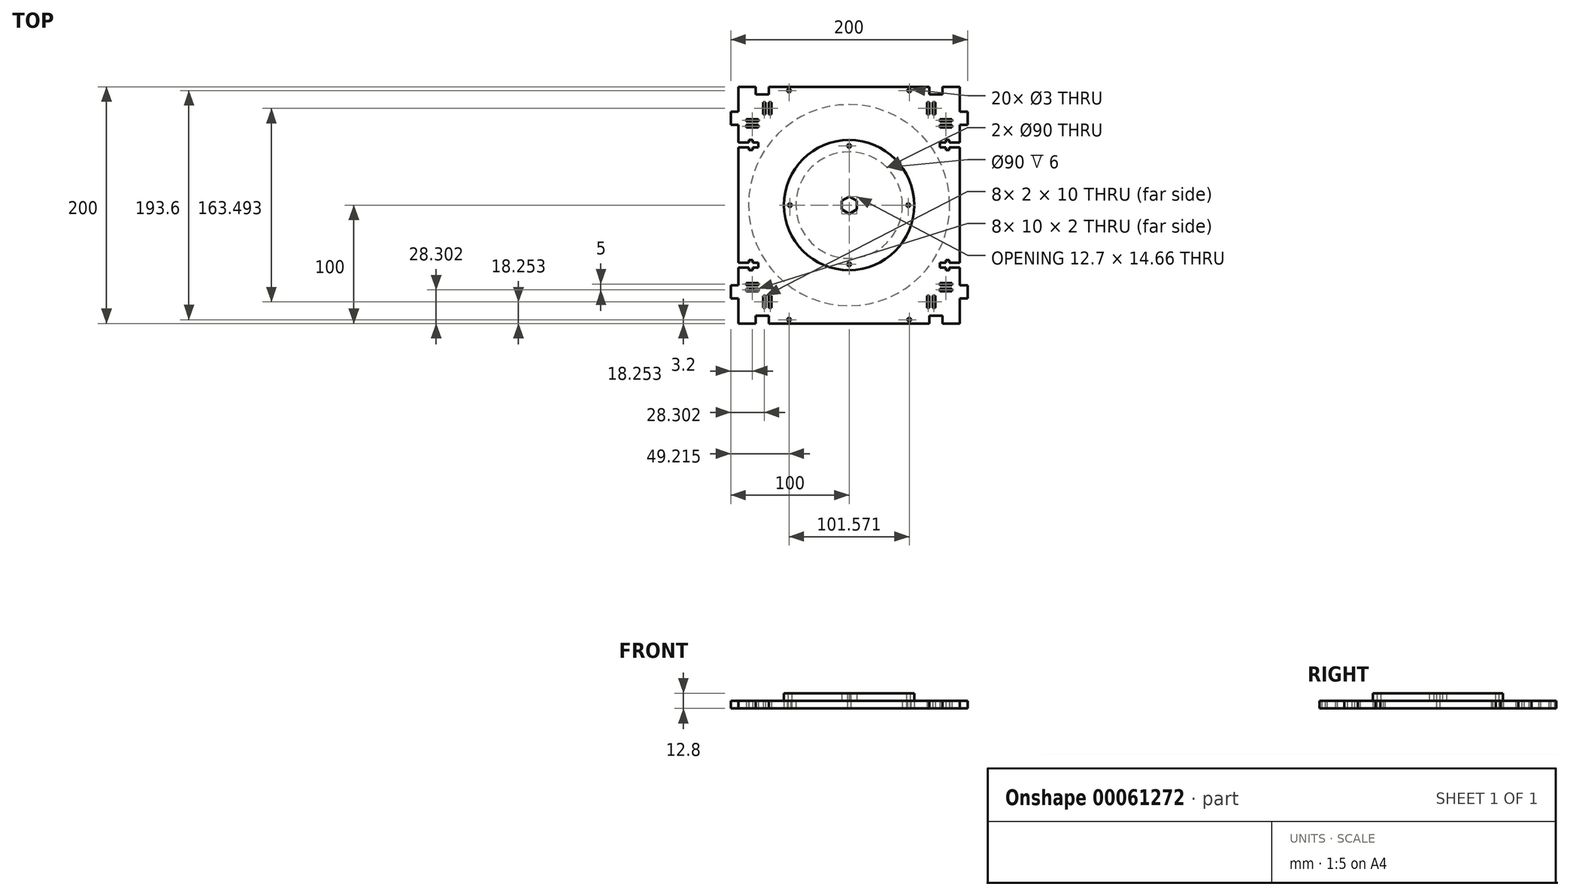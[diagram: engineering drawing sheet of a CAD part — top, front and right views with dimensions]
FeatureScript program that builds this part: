
annotation { "Feature Type Name" : "Feature", "Feature Type Description" : "" }
export const myFeature = defineFeature(function(context is Context, id is Id, definition is map)
    precondition{}
    {
        {
            var Q0;
            Q0=qCreatedBy(makeId("Top.planeOp"),FACE);
            var sketch = newSketch(context, id + "F0", { "sketchPlane" : qUnion([Q0])});
            skLineSegment(sketch, "E0.rect.bottom", {"start": v(100, 100) * mm, "end": v(-100, 100) * mm});
            skLineSegment(sketch, "E0.rect.top", {"start": v(100, -100) * mm, "end": v(-100, -100) * mm});
            skPoint(sketch, "E0.rect.middle", {"position": v(0, 0) * mm});
            skCircle(sketch, "E1", {"center": v(0, 0) * mm, "radius": 55 * mm});
            skCircle(sketch, "E2", {"center": v(0, 0) * mm, "radius": 85 * mm});
            skCircle(sketch, "E3", {"center": v(-50, 0) * mm, "radius": 1.5 * mm});
            skLineSegment(sketch, "E4", {"start": v(-55, 0) * mm, "end": v(-45, 0) * mm, "construction": true});
            skCircle(sketch, "E5.1.0", {"center": v(0, -50) * mm, "radius": 1.5 * mm});
            skCircle(sketch, "E5.2.0", {"center": v(50, 0) * mm, "radius": 1.5 * mm});
            skCircle(sketch, "E6.1.3.0", {"center": v(0, 50) * mm, "radius": 1.5 * mm});
            skLineSegment(sketch, "E7.left", {"start": v(-72.7, -76.75) * mm, "end": v(-72.7, -86.75) * mm});
            skLineSegment(sketch, "E7.right", {"start": v(-65.7, -76.75) * mm, "end": v(-65.7, -86.75) * mm});
            skLineSegment(sketch, "E8", {"start": v(0, 0) * mm, "end": v(-100, -100) * mm, "construction": true});
            skLineSegment(sketch, "E9", {"start": v(-72.7, -76.75) * mm, "end": v(-70.7, -76.75) * mm});
            skLineSegment(sketch, "E10", {"start": v(-70.7, -76.75) * mm, "end": v(-70.7, -86.75) * mm});
            skLineSegment(sketch, "E11", {"start": v(-70.7, -86.75) * mm, "end": v(-72.7, -86.75) * mm});
            skLineSegment(sketch, "E12", {"start": v(-65.7, -76.75) * mm, "end": v(-67.7, -76.75) * mm});
            skLineSegment(sketch, "E13", {"start": v(-67.7, -76.75) * mm, "end": v(-67.7, -86.75) * mm});
            skLineSegment(sketch, "E14", {"start": v(-67.7, -86.75) * mm, "end": v(-65.7, -86.75) * mm});
            skLineSegment(sketch, "E15.MirrorCS", {"start": v(-76.75, -72.7) * mm, "end": v(-76.75, -70.7) * mm});
            skLineSegment(sketch, "E16.MirrorCS", {"start": v(-76.75, -65.7) * mm, "end": v(-76.75, -67.7) * mm});
            skLineSegment(sketch, "E17.MirrorCS", {"start": v(-76.75, -65.7) * mm, "end": v(-86.75, -65.7) * mm});
            skLineSegment(sketch, "E18.MirrorCS", {"start": v(-76.75, -72.7) * mm, "end": v(-86.75, -72.7) * mm});
            skLineSegment(sketch, "E19.MirrorCS", {"start": v(-86.75, -67.7) * mm, "end": v(-86.75, -65.7) * mm});
            skLineSegment(sketch, "E20.MirrorCS", {"start": v(-76.75, -70.7) * mm, "end": v(-86.75, -70.7) * mm});
            skLineSegment(sketch, "E21.MirrorCS", {"start": v(-76.75, -67.7) * mm, "end": v(-86.75, -67.7) * mm});
            skLineSegment(sketch, "E22.MirrorCS", {"start": v(-86.75, -70.7) * mm, "end": v(-86.75, -72.7) * mm});
            skLineSegment(sketch, "E23.1.0", {"start": v(76.75, -65.7) * mm, "end": v(86.75, -65.7) * mm});
            skLineSegment(sketch, "E23.1.1", {"start": v(67.7, -76.75) * mm, "end": v(67.7, -86.75) * mm});
            skLineSegment(sketch, "E23.1.2", {"start": v(72.7, -76.75) * mm, "end": v(72.7, -86.75) * mm});
            skLineSegment(sketch, "E23.1.3", {"start": v(76.75, -72.7) * mm, "end": v(86.75, -72.7) * mm});
            skLineSegment(sketch, "E23.1.4", {"start": v(70.7, -76.75) * mm, "end": v(70.7, -86.75) * mm});
            skLineSegment(sketch, "E23.1.5", {"start": v(76.75, -67.7) * mm, "end": v(86.75, -67.7) * mm});
            skLineSegment(sketch, "E23.1.6", {"start": v(65.7, -76.75) * mm, "end": v(65.7, -86.75) * mm});
            skLineSegment(sketch, "E23.1.7", {"start": v(76.75, -70.7) * mm, "end": v(86.75, -70.7) * mm});
            skLineSegment(sketch, "E23.1.8", {"start": v(67.7, -86.75) * mm, "end": v(65.7, -86.75) * mm});
            skLineSegment(sketch, "E23.1.9", {"start": v(65.7, -76.75) * mm, "end": v(67.7, -76.75) * mm});
            skLineSegment(sketch, "E23.1.10", {"start": v(70.7, -86.75) * mm, "end": v(72.7, -86.75) * mm});
            skLineSegment(sketch, "E23.1.11", {"start": v(76.75, -72.7) * mm, "end": v(76.75, -70.7) * mm});
            skLineSegment(sketch, "E23.1.12", {"start": v(76.75, -65.7) * mm, "end": v(76.75, -67.7) * mm});
            skLineSegment(sketch, "E23.1.13", {"start": v(72.7, -76.75) * mm, "end": v(70.7, -76.75) * mm});
            skLineSegment(sketch, "E23.1.14", {"start": v(86.75, -70.7) * mm, "end": v(86.75, -72.7) * mm});
            skLineSegment(sketch, "E23.1.15", {"start": v(86.75, -67.7) * mm, "end": v(86.75, -65.7) * mm});
            skLineSegment(sketch, "E23.2.0", {"start": v(65.7, 76.75) * mm, "end": v(65.7, 86.75) * mm});
            skLineSegment(sketch, "E23.2.1", {"start": v(76.75, 67.7) * mm, "end": v(86.75, 67.7) * mm});
            skLineSegment(sketch, "E23.2.2", {"start": v(76.75, 72.7) * mm, "end": v(86.75, 72.7) * mm});
            skLineSegment(sketch, "E23.2.3", {"start": v(72.7, 76.75) * mm, "end": v(72.7, 86.75) * mm});
            skLineSegment(sketch, "E23.2.4", {"start": v(76.75, 70.7) * mm, "end": v(86.75, 70.7) * mm});
            skLineSegment(sketch, "E23.2.5", {"start": v(67.7, 76.75) * mm, "end": v(67.7, 86.75) * mm});
            skLineSegment(sketch, "E23.2.6", {"start": v(76.75, 65.7) * mm, "end": v(86.75, 65.7) * mm});
            skLineSegment(sketch, "E23.2.7", {"start": v(70.7, 76.75) * mm, "end": v(70.7, 86.75) * mm});
            skLineSegment(sketch, "E23.2.8", {"start": v(86.75, 67.7) * mm, "end": v(86.75, 65.7) * mm});
            skLineSegment(sketch, "E23.2.9", {"start": v(76.75, 65.7) * mm, "end": v(76.75, 67.7) * mm});
            skLineSegment(sketch, "E23.2.10", {"start": v(86.75, 70.7) * mm, "end": v(86.75, 72.7) * mm});
            skLineSegment(sketch, "E23.2.11", {"start": v(72.7, 76.75) * mm, "end": v(70.7, 76.75) * mm});
            skLineSegment(sketch, "E23.2.12", {"start": v(65.7, 76.75) * mm, "end": v(67.7, 76.75) * mm});
            skLineSegment(sketch, "E23.2.13", {"start": v(76.75, 72.7) * mm, "end": v(76.75, 70.7) * mm});
            skLineSegment(sketch, "E23.2.14", {"start": v(70.7, 86.75) * mm, "end": v(72.7, 86.75) * mm});
            skLineSegment(sketch, "E23.2.15", {"start": v(67.7, 86.75) * mm, "end": v(65.7, 86.75) * mm});
            skLineSegment(sketch, "E23.3.0", {"start": v(-76.75, 65.7) * mm, "end": v(-86.75, 65.7) * mm});
            skLineSegment(sketch, "E23.3.1", {"start": v(-67.7, 76.75) * mm, "end": v(-67.7, 86.75) * mm});
            skLineSegment(sketch, "E23.3.2", {"start": v(-72.7, 76.75) * mm, "end": v(-72.7, 86.75) * mm});
            skLineSegment(sketch, "E23.3.3", {"start": v(-76.75, 72.7) * mm, "end": v(-86.75, 72.7) * mm});
            skLineSegment(sketch, "E23.3.4", {"start": v(-70.7, 76.75) * mm, "end": v(-70.7, 86.75) * mm});
            skLineSegment(sketch, "E23.3.5", {"start": v(-76.75, 67.7) * mm, "end": v(-86.75, 67.7) * mm});
            skLineSegment(sketch, "E23.3.6", {"start": v(-65.7, 76.75) * mm, "end": v(-65.7, 86.75) * mm});
            skLineSegment(sketch, "E23.3.7", {"start": v(-76.75, 70.7) * mm, "end": v(-86.75, 70.7) * mm});
            skLineSegment(sketch, "E23.3.8", {"start": v(-67.7, 86.75) * mm, "end": v(-65.7, 86.75) * mm});
            skLineSegment(sketch, "E23.3.9", {"start": v(-65.7, 76.75) * mm, "end": v(-67.7, 76.75) * mm});
            skLineSegment(sketch, "E23.3.10", {"start": v(-70.7, 86.75) * mm, "end": v(-72.7, 86.75) * mm});
            skLineSegment(sketch, "E23.3.11", {"start": v(-76.75, 72.7) * mm, "end": v(-76.75, 70.7) * mm});
            skLineSegment(sketch, "E23.3.12", {"start": v(-76.75, 65.7) * mm, "end": v(-76.75, 67.7) * mm});
            skLineSegment(sketch, "E23.3.13", {"start": v(-72.7, 76.75) * mm, "end": v(-70.7, 76.75) * mm});
            skLineSegment(sketch, "E23.3.14", {"start": v(-86.75, 70.7) * mm, "end": v(-86.75, 72.7) * mm});
            skLineSegment(sketch, "E23.3.15", {"start": v(-86.75, 67.7) * mm, "end": v(-86.75, 65.7) * mm});
            skCircle(sketch, "E24", {"center": v(0, 0) * mm, "radius": 45 * mm});
            skLineSegment(sketch, "E25", {"start": v(-79, 100) * mm, "end": v(-79, 93.6) * mm});
            skLineSegment(sketch, "E26", {"start": v(-79, 93.6) * mm, "end": v(-67.81, 93.6) * mm});
            skLineSegment(sketch, "E27", {"start": v(-67.81, 93.6) * mm, "end": v(-67.81, 100) * mm});
            skLineSegment(sketch, "E28", {"start": v(0, 0) * mm, "end": v(0, 100) * mm, "construction": true});
            skLineSegment(sketch, "E29.MirrorCS", {"start": v(67.81, 93.6) * mm, "end": v(67.81, 100) * mm});
            skLineSegment(sketch, "E30.MirrorCS", {"start": v(79, 93.6) * mm, "end": v(67.81, 93.6) * mm});
            skLineSegment(sketch, "E31.MirrorCS", {"start": v(79, 100) * mm, "end": v(79, 93.6) * mm});
            skLineSegment(sketch, "E32.1.2", {"start": v(-93.6, 67.81) * mm, "end": v(-100, 67.81) * mm});
            skLineSegment(sketch, "E32.1.3", {"start": v(-100, -79) * mm, "end": v(-93.6, -79) * mm});
            skLineSegment(sketch, "E32.1.4", {"start": v(-100, 79) * mm, "end": v(-93.6, 79) * mm});
            skLineSegment(sketch, "E32.1.5", {"start": v(-93.6, -67.81) * mm, "end": v(-100, -67.81) * mm});
            skLineSegment(sketch, "E32.2.0", {"start": v(-79, -93.6) * mm, "end": v(-67.81, -93.6) * mm});
            skLineSegment(sketch, "E32.2.1", {"start": v(79, -93.6) * mm, "end": v(67.81, -93.6) * mm});
            skLineSegment(sketch, "E32.2.2", {"start": v(-67.81, -93.6) * mm, "end": v(-67.81, -100) * mm});
            skLineSegment(sketch, "E32.2.3", {"start": v(79, -100) * mm, "end": v(79, -93.6) * mm});
            skLineSegment(sketch, "E32.2.4", {"start": v(-79, -100) * mm, "end": v(-79, -93.6) * mm});
            skLineSegment(sketch, "E32.2.5", {"start": v(67.81, -93.6) * mm, "end": v(67.81, -100) * mm});
            skLineSegment(sketch, "E32.3.2", {"start": v(93.6, -67.81) * mm, "end": v(100, -67.81) * mm});
            skLineSegment(sketch, "E32.3.3", {"start": v(100, 79) * mm, "end": v(93.6, 79) * mm});
            skLineSegment(sketch, "E32.3.4", {"start": v(100, -79) * mm, "end": v(93.6, -79) * mm});
            skLineSegment(sketch, "E32.3.5", {"start": v(93.6, 67.81) * mm, "end": v(100, 67.81) * mm});
            skLineSegment(sketch, "E33", {"start": v(-100, 79) * mm, "end": v(-100, 67.81) * mm});
            skLineSegment(sketch, "E34", {"start": v(-100, -67.81) * mm, "end": v(-100, -79) * mm});
            skLineSegment(sketch, "E35", {"start": v(100, -79) * mm, "end": v(100, -67.81) * mm});
            skLineSegment(sketch, "E36", {"start": v(100, 67.81) * mm, "end": v(100, 79) * mm});
            skLineSegment(sketch, "E37", {"start": v(93.6, 67.81) * mm, "end": v(93.6, -67.81) * mm});
            skLineSegment(sketch, "E38", {"start": v(93.6, -79) * mm, "end": v(93.6, -100) * mm});
            skLineSegment(sketch, "E39", {"start": v(93.6, 79) * mm, "end": v(93.6, 100) * mm});
            skLineSegment(sketch, "E40", {"start": v(-93.6, 79) * mm, "end": v(-93.6, 100) * mm});
            skLineSegment(sketch, "E41", {"start": v(-93.6, 67.81) * mm, "end": v(-93.6, -67.81) * mm});
            skLineSegment(sketch, "E42", {"start": v(-93.6, -79) * mm, "end": v(-93.6, -100) * mm});
            skLineSegment(sketch, "E43.MirrorCS", {"start": v(81.6, -48.79) * mm, "end": v(81.6, -46.42) * mm});
            skLineSegment(sketch, "E44.MirrorCS", {"start": v(81.6, -46.42) * mm, "end": v(84.58, -46.42) * mm});
            skLineSegment(sketch, "E45.MirrorCS", {"start": v(76.6, -52.79) * mm, "end": v(76.6, -48.79) * mm});
            skLineSegment(sketch, "E46.MirrorCS", {"start": v(84.58, -55.15) * mm, "end": v(81.6, -55.15) * mm});
            skLineSegment(sketch, "E47.MirrorCS", {"start": v(84.58, -52.79) * mm, "end": v(84.58, -55.15) * mm});
            skLineSegment(sketch, "E48.MirrorCS", {"start": v(84.58, -46.42) * mm, "end": v(84.58, -48.79) * mm});
            skLineSegment(sketch, "E49.MirrorCS", {"start": v(81.6, -55.15) * mm, "end": v(81.6, -52.79) * mm});
            skLineSegment(sketch, "E50.MirrorCS", {"start": v(76.6, -48.79) * mm, "end": v(81.6, -48.79) * mm});
            skLineSegment(sketch, "E51.MirrorCS", {"start": v(84.58, -48.79) * mm, "end": v(93.6, -48.79) * mm});
            skLineSegment(sketch, "E52.MirrorCS", {"start": v(81.6, -52.79) * mm, "end": v(76.6, -52.79) * mm});
            skLineSegment(sketch, "E53.MirrorCS", {"start": v(93.6, -52.79) * mm, "end": v(84.58, -52.79) * mm});
            skLineSegment(sketch, "E54", {"start": v(-93.6, 0) * mm, "end": v(93.6, 0) * mm, "construction": true});
            skLineSegment(sketch, "E55", {"start": v(93.6, -48.79) * mm, "end": v(93.6, -52.79) * mm});
            skLineSegment(sketch, "E56.MirrorCS", {"start": v(93.6, 52.79) * mm, "end": v(84.58, 52.79) * mm});
            skLineSegment(sketch, "E57.MirrorCS", {"start": v(81.6, 55.15) * mm, "end": v(81.6, 52.79) * mm});
            skLineSegment(sketch, "E58.MirrorCS", {"start": v(81.6, 48.79) * mm, "end": v(81.6, 46.42) * mm});
            skLineSegment(sketch, "E59.MirrorCS", {"start": v(76.6, 48.79) * mm, "end": v(81.6, 48.79) * mm});
            skLineSegment(sketch, "E60.MirrorCS", {"start": v(84.58, 48.79) * mm, "end": v(93.6, 48.79) * mm});
            skLineSegment(sketch, "E61.MirrorCS", {"start": v(81.6, 52.79) * mm, "end": v(76.6, 52.79) * mm});
            skLineSegment(sketch, "E62.MirrorCS", {"start": v(84.58, 55.15) * mm, "end": v(81.6, 55.15) * mm});
            skLineSegment(sketch, "E63.MirrorCS", {"start": v(76.6, 52.79) * mm, "end": v(76.6, 48.79) * mm});
            skLineSegment(sketch, "E64.MirrorCS", {"start": v(84.58, 52.79) * mm, "end": v(84.58, 55.15) * mm});
            skLineSegment(sketch, "E65.MirrorCS", {"start": v(93.6, 48.79) * mm, "end": v(93.6, 52.79) * mm});
            skLineSegment(sketch, "E66.MirrorCS", {"start": v(84.58, 46.42) * mm, "end": v(84.58, 48.79) * mm});
            skLineSegment(sketch, "E67.MirrorCS", {"start": v(81.6, 46.42) * mm, "end": v(84.58, 46.42) * mm});
            skPoint(sketch, "E68", {"position": v(93.6, 0) * mm});
            skCircle(sketch, "E69", {"center": v(-50.79, 96.8) * mm, "radius": 1.5 * mm});
            skPoint(sketch, "E70", {"position": v(-67.81, 96.8) * mm});
            skLineSegment(sketch, "E71", {"start": v(-50.79, 96.8) * mm, "end": v(-67.81, 96.8) * mm, "construction": true});
            skLineSegment(sketch, "E72.MirrorCS", {"start": v(-84.58, 48.79) * mm, "end": v(-93.6, 48.79) * mm});
            skLineSegment(sketch, "E73.MirrorCS", {"start": v(-81.6, 46.42) * mm, "end": v(-84.58, 46.42) * mm});
            skLineSegment(sketch, "E74.MirrorCS", {"start": v(-76.6, 48.79) * mm, "end": v(-81.6, 48.79) * mm});
            skLineSegment(sketch, "E75.MirrorCS", {"start": v(-84.58, 46.42) * mm, "end": v(-84.58, 48.79) * mm});
            skLineSegment(sketch, "E76.MirrorCS", {"start": v(-81.6, 55.15) * mm, "end": v(-81.6, 52.79) * mm});
            skLineSegment(sketch, "E77.MirrorCS", {"start": v(-93.6, 52.79) * mm, "end": v(-84.58, 52.79) * mm});
            skLineSegment(sketch, "E78.MirrorCS", {"start": v(-84.58, 55.15) * mm, "end": v(-81.6, 55.15) * mm});
            skLineSegment(sketch, "E79.MirrorCS", {"start": v(-76.6, 52.79) * mm, "end": v(-76.6, 48.79) * mm});
            skLineSegment(sketch, "E80.MirrorCS", {"start": v(-93.6, 48.79) * mm, "end": v(-93.6, 52.79) * mm});
            skLineSegment(sketch, "E81.MirrorCS", {"start": v(-81.6, 48.79) * mm, "end": v(-81.6, 46.42) * mm});
            skLineSegment(sketch, "E82.MirrorCS", {"start": v(-81.6, 52.79) * mm, "end": v(-76.6, 52.79) * mm});
            skLineSegment(sketch, "E83.MirrorCS", {"start": v(-84.58, 52.79) * mm, "end": v(-84.58, 55.15) * mm});
            skLineSegment(sketch, "E84.MirrorCS", {"start": v(-93.6, -52.79) * mm, "end": v(-84.58, -52.79) * mm});
            skLineSegment(sketch, "E85.MirrorCS", {"start": v(-76.6, -52.79) * mm, "end": v(-76.6, -48.79) * mm});
            skLineSegment(sketch, "E86.MirrorCS", {"start": v(-84.58, -48.79) * mm, "end": v(-93.6, -48.79) * mm});
            skLineSegment(sketch, "E87.MirrorCS", {"start": v(-84.58, -52.79) * mm, "end": v(-84.58, -55.15) * mm});
            skLineSegment(sketch, "E88.MirrorCS", {"start": v(-81.6, -48.79) * mm, "end": v(-81.6, -46.42) * mm});
            skLineSegment(sketch, "E89.MirrorCS", {"start": v(-81.6, -55.15) * mm, "end": v(-81.6, -52.79) * mm});
            skLineSegment(sketch, "E90.MirrorCS", {"start": v(-93.6, -48.79) * mm, "end": v(-93.6, -52.79) * mm});
            skLineSegment(sketch, "E91.MirrorCS", {"start": v(-81.6, -46.42) * mm, "end": v(-84.58, -46.42) * mm});
            skLineSegment(sketch, "E92.MirrorCS", {"start": v(-84.58, -55.15) * mm, "end": v(-81.6, -55.15) * mm});
            skLineSegment(sketch, "E93.MirrorCS", {"start": v(-76.6, -48.79) * mm, "end": v(-81.6, -48.79) * mm});
            skLineSegment(sketch, "E94.MirrorCS", {"start": v(-84.58, -46.42) * mm, "end": v(-84.58, -48.79) * mm});
            skLineSegment(sketch, "E95.MirrorCS", {"start": v(-81.6, -52.79) * mm, "end": v(-76.6, -52.79) * mm});
            skPoint(sketch, "E96", {"position": v(93.6, -50.79) * mm});
            skLineSegment(sketch, "E97", {"start": v(93.6, -50.79) * mm, "end": v(93.6, -67.81) * mm});
            skCircle(sketch, "E98.MirrorC", {"center": v(50.79, 96.8) * mm, "radius": 1.5 * mm});
            skCircle(sketch, "E99.MirrorC", {"center": v(50.79, -96.8) * mm, "radius": 1.5 * mm});
            skCircle(sketch, "E100.MirrorC", {"center": v(-50.79, -96.8) * mm, "radius": 1.5 * mm});
            skCircle(sketch, "E101.cCircle", {"center": v(0, 0) * mm, "radius": 7.33 * mm, "construction": true});
            skLineSegment(sketch, "E101.0", {"start": v(0, 7.33) * mm, "end": v(6.35, 3.67) * mm});
            skLineSegment(sketch, "E101.1", {"start": v(6.35, 3.67) * mm, "end": v(6.35, -3.67) * mm});
            skLineSegment(sketch, "E101.2", {"start": v(6.35, -3.67) * mm, "end": v(0, -7.33) * mm});
            skLineSegment(sketch, "E101.3", {"start": v(0, -7.33) * mm, "end": v(-6.35, -3.67) * mm});
            skLineSegment(sketch, "E101.4", {"start": v(-6.35, -3.67) * mm, "end": v(-6.35, 3.67) * mm});
            skLineSegment(sketch, "E101.5", {"start": v(-6.35, 3.67) * mm, "end": v(0, 7.33) * mm});
            skLineSegment(sketch, "E102", {"start": v(-100, 100) * mm, "end": v(-93.6, 100) * mm});
            skLineSegment(sketch, "E103", {"start": v(-100, 100) * mm, "end": v(-100, -100) * mm, "construction": true});
            skSolve(sketch);
        }
        {
            var Q0;
            Q0=makeQuery(id+"F0.imprint","IMPRINT",FACE,{"disambiguationData":[TD([[makeQuery(id+"F0.imprint","IMPRINT",EDGE,{"derivedFrom":sQuery(id+"F0.wireOp",EDGE,"E24")}),1.0]])]});
            var Q1;
            Q1=makeQuery(id+"F0.imprint","IMPRINT",FACE,{"disambiguationData":[TD([[makeQuery(id+"F0.imprint","IMPRINT",EDGE,{"derivedFrom":sQuery(id+"F0.wireOp",EDGE,"E1")}),1.0]])]});
            extrude(context, id + "F1", {"entities" : qUnion([Q0, Q1]), "depth" : 6.4 * mm});
        }
        {
            var Q0;
            Q0=makeQuery(id+"F0.imprint","IMPRINT",FACE,{"disambiguationData":[TD([[makeQuery(id+"F0.imprint","IMPRINT",EDGE,{"derivedFrom":sQuery(id+"F0.wireOp",EDGE,"E1")}),1.0]])]});
            extrude(context, id + "F2", {"entities" : qUnion([Q0]), "depth" : 6 * mm});
        }
        {
            var Q0;
            Q0=makeQuery(id+"F0.imprint","IMPRINT",FACE,{"disambiguationData":[TD([[makeQuery(id+"F0.imprint","IMPRINT",EDGE,{"derivedFrom":sQuery(id+"F0.wireOp",EDGE,"E1")}),-1.0]])]});
            var Q1;
            Q1=makeQuery(id+"F0.imprint","IMPRINT",FACE,{"disambiguationData":[TD([[makeQuery(id+"F0.imprint","IMPRINT",EDGE,{"derivedFrom":sQuery(id+"F0.wireOp",EDGE,"E1")}),1.0]])]});
            extrude(context, id + "F3", {"entities" : qUnion([Q0, Q1]), "depth" : 6 * mm});
        }
        {
            var Q0;
            Q0=makeQuery(id+"F0.imprint","IMPRINT",FACE,{"disambiguationData":[TD([[makeQuery(id+"F0.imprint","IMPRINT",EDGE,{"derivedFrom":sQuery(id+"F0.wireOp",EDGE,"E2")}),-1.0]])]});
            var Q1;
            Q1=makeQuery(id+"F0.imprint","IMPRINT",FACE,{"disambiguationData":[TD([[makeQuery(id+"F0.imprint","IMPRINT",EDGE,{"derivedFrom":sQuery(id+"F0.wireOp",EDGE,"E1")}),-1.0]])]});
            var Q2;
            Q2=makeQuery(id+"F0.imprint","IMPRINT",FACE,{"disambiguationData":[TD([[makeQuery(id+"F0.imprint","IMPRINT",EDGE,{"derivedFrom":sQuery(id+"F0.wireOp",EDGE,"E1")}),1.0]])]});
            extrude(context, id + "F4", {"entities" : qUnion([Q0, Q1, Q2]), "depth" : 6.4 * mm});
        }
        {
            var Q0;
            Q0=makeQuery(id+"F1.opExtrude","SWEPT_BODY",BODY,{"disambiguationData":[OSD([sQuery(id+"F0.wireOp",EDGE,"E1"),sQuery(id+"F0.wireOp",EDGE,"E3"),sQuery(id+"F0.wireOp",EDGE,"E5.1.0"),sQuery(id+"F0.wireOp",EDGE,"E5.2.0"),sQuery(id+"F0.wireOp",EDGE,"E6.1.3.0"),sQuery(id+"F0.wireOp",EDGE,"E101.0"),sQuery(id+"F0.wireOp",EDGE,"E101.1"),sQuery(id+"F0.wireOp",EDGE,"E101.2"),sQuery(id+"F0.wireOp",EDGE,"E101.3"),sQuery(id+"F0.wireOp",EDGE,"E101.4"),sQuery(id+"F0.wireOp",EDGE,"E101.5")])]});
            var Q1;
            Q1=makeQuery(id+"F4.opExtrude","SWEPT_EDGE",EDGE,{"disambiguationData":[OSD([sQuery(id+"F0.wireOp",EDGE,"E41"),sQuery(id+"F0.wireOp",EDGE,"E77.MirrorCS"),sQuery(id+"F0.wireOp",EDGE,"E80.MirrorCS")])]});
            transform(context, id + "F5", {"entities" : qUnion([Q0]), "transformType" : TransformType.TRANSLATION_ENTITY, "oppositeDirectionEntity" : true, "transformLine" : qUnion([Q1]), "makeCopy" : false});
        }
    });
